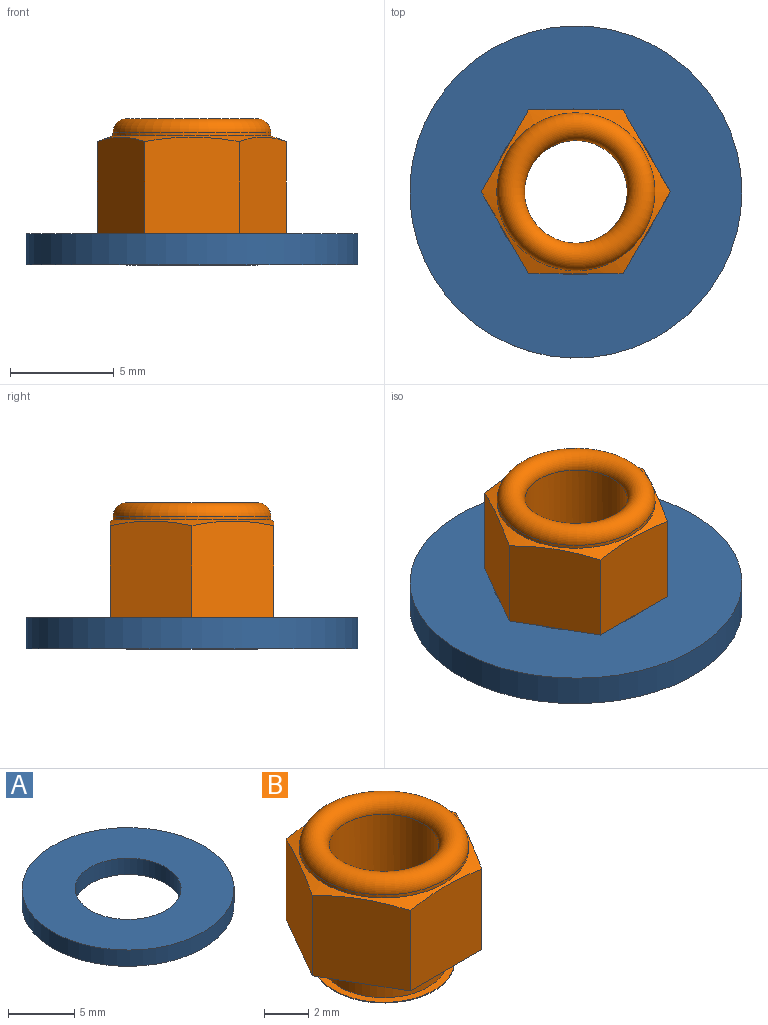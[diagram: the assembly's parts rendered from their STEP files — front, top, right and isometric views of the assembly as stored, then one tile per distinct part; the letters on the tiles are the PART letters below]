
ASSEMBLY  parts=2 mates=1
PART A: 4 faces, bbox 16x16x1.5 mm
  f0: cylinder r=4mm len=8mm, axis (0,0,-1), area 37.7mm2, adj f2,f3
  f1: cylinder r=8mm len=16mm, axis (0,0,-1), area 75.4mm2, adj f2,f3
  f2: plane 16x16mm, normal (0,0,1), area 150.8mm2, adj f0,f1
  f3: plane 16x16mm, normal (0,0,-1), area 150.8mm2, adj f0,f1
PART B: 15 faces, bbox 9.1x9.1x7.1 mm
  f0: plane 4.65x4.56mm, normal (0,-1,0), area 20.8mm2, adj f1,f5,f10,f12
  f1: plane 4.65x3.95mm, normal (0.87,-0.5,0), area 20.8mm2, adj f0,f2,f10,f12
  f2: plane 4.65x3.95mm, normal (0.87,0.5,0), area 20.8mm2, adj f1,f3,f10,f12
  f3: plane 4.65x4.56mm, normal (0,1,0), area 20.8mm2, adj f2,f4,f10,f12
  f4: plane 4.65x3.95mm, normal (-0.87,0.5,0), area 20.8mm2, adj f3,f5,f10,f12
  f5: plane 4.65x3.95mm, normal (-0.87,-0.5,0), area 20.8mm2, adj f0,f4,f10,f12
  f6: cylinder r=2.81mm len=5.61mm, axis (0,0,1), area 26.4mm2, adj f7,f10
  f7: plane 6.34x6.34mm, normal (0,0,1), area 6.8mm2, adj f6,f8
  f8: cylinder r=3.17mm len=6.34mm, axis (0,0,1), area 0.7mm2, adj f7,f9
  f9: plane 6.34x6.34mm, normal (0,0,-1), area 12.3mm2, adj f8,f11
  f10: plane 9.11x7.89mm, normal (0,0,-1), area 29.2mm2, adj f0,f1,f2,f3,f4,f5,f6
  f11: cylinder r=2.48mm len=6.41mm, axis (0,0,1), area 99.6mm2, adj f9,f13
  f12: cone r=3.81mm half-angle=70deg, axis (0,0,-1), area 8.9mm2, adj f0,f1,f2,f3,f4,f5,f14
  f13: torus R=3.14mm, axis (0,0,1), area 41.2mm2, adj f11,f14
  f14: cylinder r=3.8mm len=7.61mm, axis (0,0,1), area 4mm2, adj f12,f13
PLACE A t=(0.38,0.73,0.73)mm
PLACE B t=(0.38,0.73,0.73)mm
MATE fastened A.f1 <-> B.f6  axis (0,0,-1) through (0.38,0.73,0.73)mm
